# Revit family: ToiletRollHolder_SurfaceMount_Nero_Mecca_Shelf
name_source: partatom
category: Specialty Equipment
units: mm (PartAtom-declared; Revit-internal decimal feet)

## family parameters
Always vertical = Yes
Cut with Voids When Loaded = Yes
Maintain Annotation Orientation = No
OmniClass Number = 23.31.25.21
OmniClass Title = Toilet Paper Dispensers
Part Type = Normal
Room Calculation Point = No
Round Connector Dimension = Use Diameter
Shared = No
Work Plane-Based = No

## types (7) — shared parameters
Assembly Code = C1030220
Default Elevation = 1050 mm
IfcExportAs = IfcFurnitureType
IfcExportType = USERDEFINED
Manufacturer = Nero
ManufacturerOverallDepth = 100 mm  [stored 0.328084 ft]
ManufacturerOverallHeight = 100 mm  [stored 0.328084 ft]
ManufacturerOverallWidth = 300 mm  [stored 0.984252 ft]
ManufacturerURLProductSpecific = https://nerotapware.com.au
ModifiedIssue = 20251105 $
URL = https://nerotapware.com.au
Uniclass2015Code = Pr_40_20_76_88
Uniclass2015Title = Toilet roll holders
Uniclass2015Version = Products v1.35

## per-type parameters (varying)
| type | Description | ManufacturerSpecCode | Material | Model | Type Comments |
| Matte White (NR1986EMW) | Mecca Double Toilet Roll Holder With Shelf Matte White | NR1986EMW | Metal_MatteWhite_Nero | NR1986EMW | Toilet Roll Holder - Surface Mount - Shelf - Matte White |
| Matte Black (NR1986EMB) | Mecca Double Toilet Roll Holder With Shelf Matte Black | NR1986EMB | Metal_MatteBlack_Nero | NR1986EMB | Toilet Roll Holder - Surface Mount - Shelf - Matte Black |
| Brushed Gold (NR1986EBG) | Mecca Double Toilet Roll Holder With Shelf Brushed Gold | NR1986EBG | Metal_Gold_Nero_Brushed | NR1986EBG | Toilet Roll Holder - Surface Mount - Shelf - Brushed Gold |
| Brushed Bronze (NR1986EBZ) | Mecca Double Toilet Roll Holder With Shelf Brushed Bronze | NR1986EBZ | Metal_Bronze_Nero_Brushed | NR1986EBZ | Toilet Roll Holder - Surface Mount - Shelf - Brushed Bronze |
| Brushed Nickel (NR1986EBN) | Mecca Double Toilet Roll Holder With Shelf Brushed Nickel | NR1986EBN | Metal_Nickel_Nero_Brushed | NR1986EBN | Toilet Roll Holder - Surface Mount - Shelf - Brushed Nickel |
| Gunmetal (NR1986EGM) | Mecca Double Toilet Roll Holder With Shelf Gun Metal | NR1986EGM | Metal_GunMetal_Nero | NR1986EGM | Toilet Roll Holder - Surface Mount - Shelf - Gunmetal |
| Chrome (NR1986ECH) | Mecca Double Toilet Roll Holder With Shelf Chrome | NR1986ECH | Metal_Chrome_Nero | NR1986ECH | Toilet Roll Holder - Surface Mount - Shelf - Chrome |

note: [stored X ft] marks values corroborated as IEEE doubles in the binary element streams (Revit-internal decimal feet)

## geometry (parser evidence)
native form markers: Sweep x2
no freeform markers — native parametric forms only
